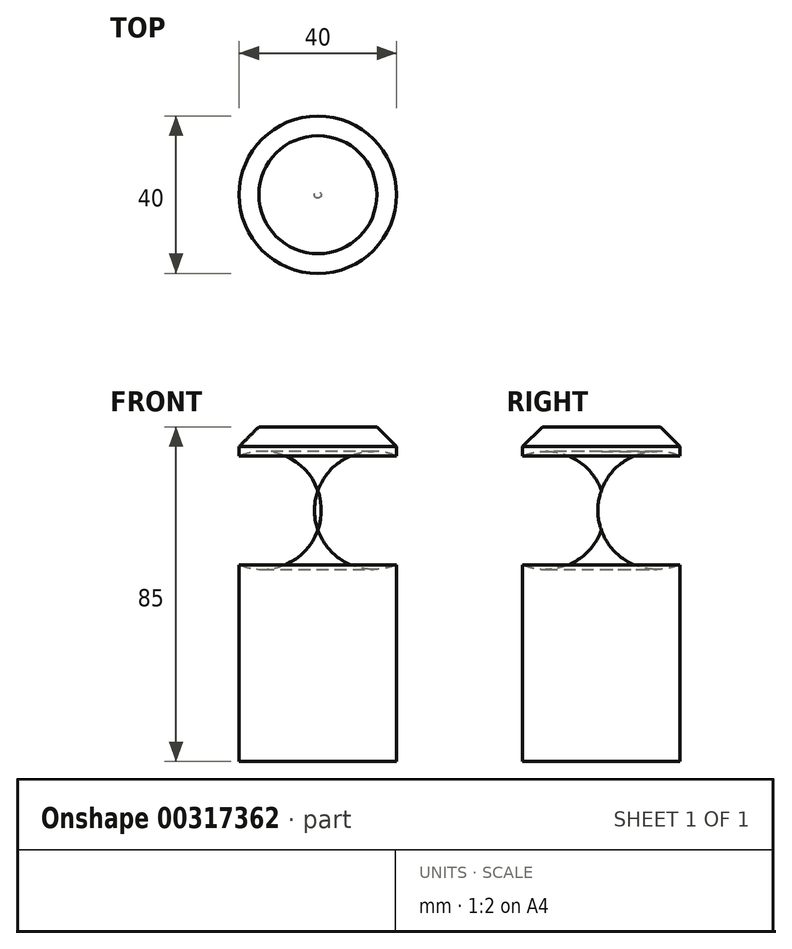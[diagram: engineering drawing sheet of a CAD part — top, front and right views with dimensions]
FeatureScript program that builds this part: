
annotation { "Feature Type Name" : "Feature", "Feature Type Description" : "" }
export const myFeature = defineFeature(function(context is Context, id is Id, definition is map)
    precondition{}
    {
        {
            var Q0;
            Q0=qCreatedBy(makeId("Front.planeOp"),FACE);
            var sketch = newSketch(context, id + "F0", { "sketchPlane" : qUnion([Q0])});
            skLineSegment(sketch, "E0", {"start": v(0, 0) * mm, "end": v(0, 85) * mm});
            skLineSegment(sketch, "E1", {"start": v(0, 85) * mm, "end": v(20, 85) * mm});
            skLineSegment(sketch, "E2", {"start": v(20, 85) * mm, "end": v(20, 77.6) * mm});
            skArc(sketch, "E3", {"start": v(20, 50) * mm, "mid": v(29.13, 63.8) * mm, "end": v(20, 77.6) * mm});
            skLineSegment(sketch, "E4", {"start": v(20, 50) * mm, "end": v(20, 0) * mm});
            skLineSegment(sketch, "E5", {"start": v(20, 0) * mm, "end": v(0, 0) * mm});
            skSolve(sketch);
        }
        {
            var Q0;
            Q0=makeQuery(id+"F0.imprint","IMPRINT",FACE,{"disambiguationData":[TD([[makeQuery(id+"F0.imprint","IMPRINT",EDGE,{"derivedFrom":sQuery(id+"F0.wireOp",EDGE,"E0")}),-1.0]])]});
            var Q1;
            Q1=sQuery(id+"F0.wireOp",EDGE,"E0");
            revolve(context, id + "F1", {"entities" : qUnion([Q0]), "axis" : qUnion([Q1]), "revolveType" : RevolveType.FULL});
        }
        {
            var Q0;
            Q0=qCreatedBy(makeId("Front.planeOp"),FACE);
            var sketch = newSketch(context, id + "F2", { "sketchPlane" : qUnion([Q0])});
            skEllipse(sketch, "E6", {"center": v(120, 105) * mm, "majorRadius": 17.5 * mm, "minorRadius": 15 * mm, "majorAxis": v(1, 0)});
            skLineSegment(sketch, "E7", {"start": v(0, 104.86) * mm, "end": v(0, -14.36) * mm});
            skSolve(sketch);
        }
        {
            var Q0;
            Q0=makeQuery(id+"F2.imprint","IMPRINT",FACE,{"disambiguationData":[TD([[makeQuery(id+"F2.imprint","IMPRINT",EDGE,{"derivedFrom":sQuery(id+"F2.wireOp",EDGE,"E6")}),1.0]])]});
            var Q1;
            Q1=sQuery(id+"F2.wireOp",EDGE,"E7");
            revolve(context, id + "F3", {"entities" : qUnion([Q0]), "axis" : qUnion([Q1]), "revolveType" : RevolveType.FULL});
        }
        {
            var Q0;
            Q0=qCreatedBy(makeId("Front.planeOp"),FACE);
            var sketch = newSketch(context, id + "F4", { "sketchPlane" : qUnion([Q0])});
            skLineSegment(sketch, "E8", {"start": v(0, 63.8) * mm, "end": v(33.83, 63.8) * mm});
            skArc(sketch, "E9", {"start": v(33.83, 63.8) * mm, "mid": v(53.22, 69.38) * mm, "end": v(66.68, 84.4) * mm});
            skArc(sketch, "E10", {"start": v(66.68, 84.4) * mm, "mid": v(80.14, 99.42) * mm, "end": v(99.52, 105) * mm});
            skLineSegment(sketch, "E11", {"start": v(99.52, 105) * mm, "end": v(120, 105) * mm});
            skSolve(sketch);
        }
        {
            var Q0;
            Q0=qCreatedBy(makeId("Right.planeOp"),FACE);
            var sketch = newSketch(context, id + "F5", { "sketchPlane" : qUnion([Q0])});
            skEllipse(sketch, "E12", {"center": v(0, 63.8) * mm, "majorRadius": 12.5 * mm, "minorRadius": 10 * mm, "majorAxis": v(1, 0)});
            skSolve(sketch);
        }
        {
            var Q0;
            Q0=makeQuery(id+"F5.imprint","IMPRINT",FACE,{"disambiguationData":[TD([[makeQuery(id+"F5.imprint","IMPRINT",EDGE,{"derivedFrom":sQuery(id+"F5.wireOp",EDGE,"E12")}),1.0]])]});
            var Q1;
            Q1=sQuery(id+"F4.wireOp",EDGE,"E8");
            var Q2;
            Q2=sQuery(id+"F4.wireOp",EDGE,"E9");
            var Q3;
            Q3=sQuery(id+"F4.wireOp",EDGE,"E10");
            var Q4;
            Q4=sQuery(id+"F4.wireOp",EDGE,"E11");
            sweep(context, id + "F6", {"profiles" : qUnion([Q0]), "path" : qUnion([Q1, Q2, Q3, Q4])});
        }
        {
            var Q0;
            Q0=makeQuery(id+"F6.opSweep","SWEPT_BODY",BODY,{"disambiguationData":[OSD([sQuery(id+"F4.wireOp",EDGE,"E11"),sQuery(id+"F5.wireOp",EDGE,"E12")])]});
            var Q1;
            Q1=sQuery(id+"F2.wireOp",EDGE,"E7");
            circularPattern(context, id + "F7", {"operationType" : NewBodyOperationType.ADD, "entities" : qUnion([Q0]), "axis" : qUnion([Q1]), "angle" : 360 * degree, "instanceCount" : 4, "equalSpace" : true});
        }
        {
            var Q0;
            Q0=makeQuery(id+"F1.opRevolve","SWEPT_EDGE",EDGE,{"disambiguationData":[OSD([sQuery(id+"F0.wireOp",EDGE,"E1"),sQuery(id+"F0.wireOp",EDGE,"E2")])]});
            chamfer(context, id + "F8", {"entities" : qUnion([Q0]), "width" : 5 * mm, "tangentPropagation" : true});
        }
        {
            var Q0;
            Q0=makeQuery(id+"F7.boolean.opBoolean","INTERSECT",EDGE,{"derivedFrom":[makeQuery(id+"F3.opRevolve","SWEPT_FACE",FACE,{"disambiguationData":[OSD([sQuery(id+"F2.wireOp",EDGE,"E6")])]}),makeQuery(id+"F7.opPattern","COPY",FACE,{"derivedFrom":makeQuery(id+"F6.opSweep","SWEPT_FACE",FACE,{"disambiguationData":[OSD([sQuery(id+"F4.wireOp",EDGE,"E11"),sQuery(id+"F5.wireOp",EDGE,"E12")])]}),"instanceName":"2"})]});
            var Q1;
            Q1=makeQuery(id+"F7.boolean.opBoolean","INTERSECT",EDGE,{"derivedFrom":[makeQuery(id+"F3.opRevolve","SWEPT_FACE",FACE,{"disambiguationData":[OSD([sQuery(id+"F2.wireOp",EDGE,"E6")])]}),makeQuery(id+"F7.opPattern","COPY",FACE,{"derivedFrom":makeQuery(id+"F6.opSweep","SWEPT_FACE",FACE,{"disambiguationData":[OSD([sQuery(id+"F4.wireOp",EDGE,"E11"),sQuery(id+"F5.wireOp",EDGE,"E12")])]}),"instanceName":"3"})]});
            var Q2;
            Q2=makeQuery(id+"F7.boolean.opBoolean","INTERSECT",EDGE,{"derivedFrom":[makeQuery(id+"F3.opRevolve","SWEPT_FACE",FACE,{"disambiguationData":[OSD([sQuery(id+"F2.wireOp",EDGE,"E6")])]}),makeQuery(id+"F7.opPattern","COPY",FACE,{"derivedFrom":makeQuery(id+"F6.opSweep","SWEPT_FACE",FACE,{"disambiguationData":[OSD([sQuery(id+"F4.wireOp",EDGE,"E11"),sQuery(id+"F5.wireOp",EDGE,"E12")])]}),"instanceName":"1"})]});
            var Q3;
            Q3=makeQuery(id+"F7.boolean.opBoolean","INTERSECT",EDGE,{"derivedFrom":[makeQuery(id+"F3.opRevolve","SWEPT_FACE",FACE,{"disambiguationData":[OSD([sQuery(id+"F2.wireOp",EDGE,"E6")])]}),makeQuery(id+"F6.opSweep","SWEPT_FACE",FACE,{"disambiguationData":[OSD([sQuery(id+"F4.wireOp",EDGE,"E11"),sQuery(id+"F5.wireOp",EDGE,"E12")])]})]});
            fillet(context, id + "F9", {"entities" : qUnion([Q0, Q1, Q2, Q3]), "radius" : 5 * mm, "tangentPropagation" : true, "allowEdgeOverflow" : false});
        }
        {
            var Q0;
            Q0=makeQuery(id+"F7.boolean.opBoolean","INTERSECT",EDGE,{"derivedFrom":[makeQuery(id+"F1.opRevolve","SWEPT_FACE",FACE,{"disambiguationData":[OSD([sQuery(id+"F0.wireOp",EDGE,"E3")])]}),makeQuery(id+"F7.opPattern","COPY",FACE,{"derivedFrom":makeQuery(id+"F6.opSweep","SWEPT_FACE",FACE,{"disambiguationData":[OSD([sQuery(id+"F4.wireOp",EDGE,"E8"),sQuery(id+"F5.wireOp",EDGE,"E12")])]}),"instanceName":"1"})]});
            var Q1;
            Q1=makeQuery(id+"F7.boolean.opBoolean","INTERSECT",EDGE,{"derivedFrom":[makeQuery(id+"F1.opRevolve","SWEPT_FACE",FACE,{"disambiguationData":[OSD([sQuery(id+"F0.wireOp",EDGE,"E3")])]}),makeQuery(id+"F7.opPattern","COPY",FACE,{"derivedFrom":makeQuery(id+"F6.opSweep","SWEPT_FACE",FACE,{"disambiguationData":[OSD([sQuery(id+"F4.wireOp",EDGE,"E8"),sQuery(id+"F5.wireOp",EDGE,"E12")])]}),"instanceName":"2"})]});
            var Q2;
            Q2=makeQuery(id+"F7.boolean.opBoolean","INTERSECT",EDGE,{"derivedFrom":[makeQuery(id+"F1.opRevolve","SWEPT_FACE",FACE,{"disambiguationData":[OSD([sQuery(id+"F0.wireOp",EDGE,"E3")])]}),makeQuery(id+"F7.opPattern","COPY",FACE,{"derivedFrom":makeQuery(id+"F6.opSweep","SWEPT_FACE",FACE,{"disambiguationData":[OSD([sQuery(id+"F4.wireOp",EDGE,"E8"),sQuery(id+"F5.wireOp",EDGE,"E12")])]}),"instanceName":"3"})]});
            var Q3;
            Q3=makeQuery(id+"F7.boolean.opBoolean","INTERSECT",EDGE,{"derivedFrom":[makeQuery(id+"F1.opRevolve","SWEPT_FACE",FACE,{"disambiguationData":[OSD([sQuery(id+"F0.wireOp",EDGE,"E3")])]}),makeQuery(id+"F6.opSweep","SWEPT_FACE",FACE,{"disambiguationData":[OSD([sQuery(id+"F4.wireOp",EDGE,"E8"),sQuery(id+"F5.wireOp",EDGE,"E12")])]})]});
            fillet(context, id + "F10", {"entities" : qUnion([Q0, Q1, Q2, Q3]), "radius" : 10 * mm, "tangentPropagation" : true, "allowEdgeOverflow" : false});
        }
    });
